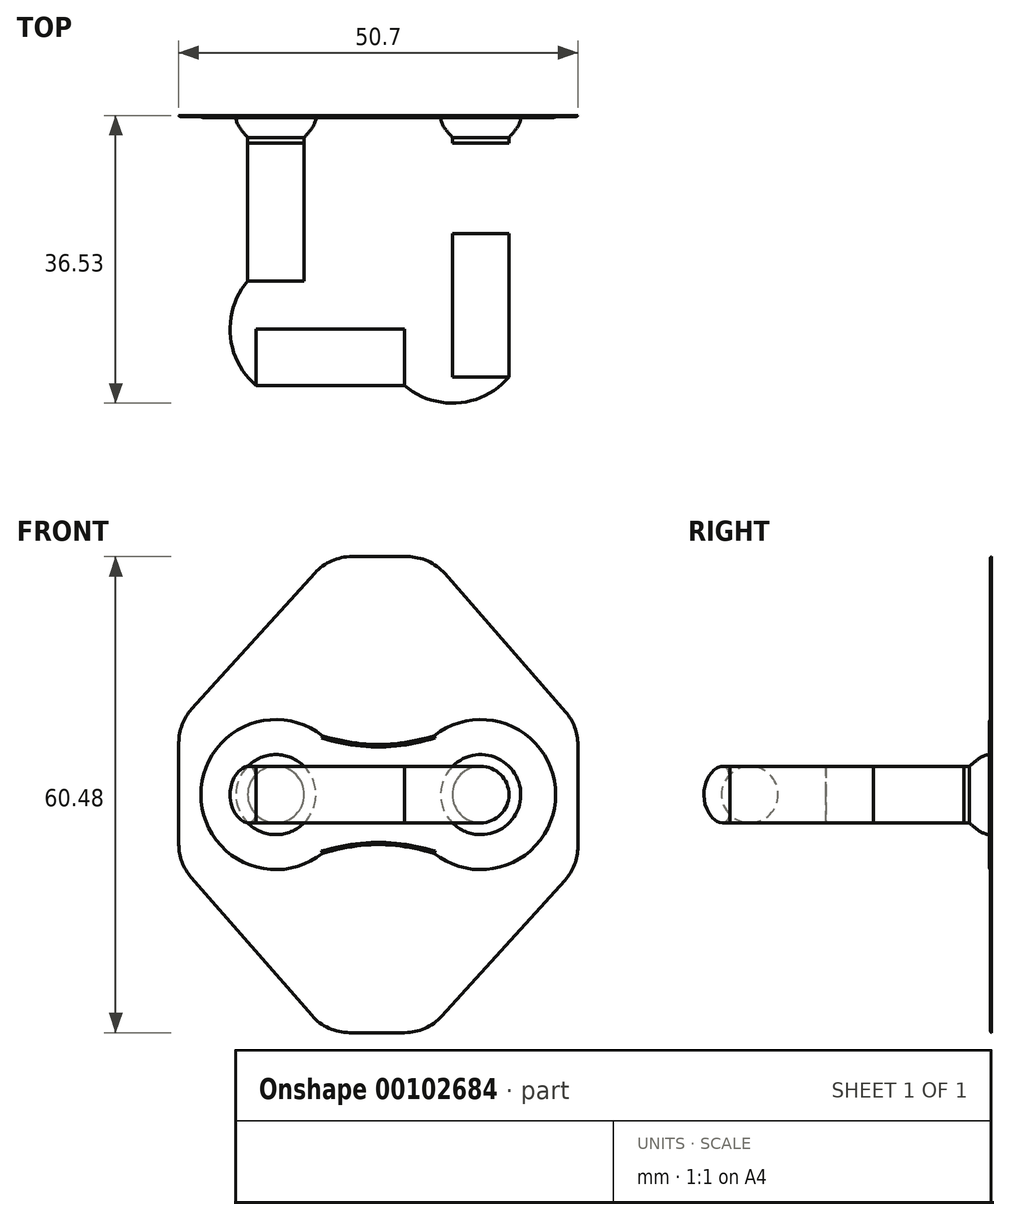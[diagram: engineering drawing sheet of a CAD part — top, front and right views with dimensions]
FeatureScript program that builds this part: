
annotation { "Feature Type Name" : "Feature", "Feature Type Description" : "" }
export const myFeature = defineFeature(function(context is Context, id is Id, definition is map)
    precondition{}
    {
        {
            var Q0;
            Q0=qCreatedBy(makeId("Front.planeOp"),FACE);
            var sketch = newSketch(context, id + "F0", { "sketchPlane" : qUnion([Q0])});
            skLineSegment(sketch, "E0.bottom", {"start": v(-25.35, 30.24) * mm, "end": v(-6.16, 30.24) * mm, "construction": true});
            skLineSegment(sketch, "E0.top", {"start": v(-25.35, -30.24) * mm, "end": v(-6.54, -30.24) * mm, "construction": true});
            skLineSegment(sketch, "E0.left", {"start": v(-25.35, 30.24) * mm, "end": v(-25.35, 9.06) * mm, "construction": true});
            skLineSegment(sketch, "E0.right", {"start": v(25.35, 30.24) * mm, "end": v(25.35, 8.72) * mm, "construction": true});
            skLineSegment(sketch, "E1", {"start": v(-25.35, 30.24) * mm, "end": v(-16.12, 19.24) * mm, "construction": true});
            skLineSegment(sketch, "E2", {"start": v(25.35, 30.24) * mm, "end": v(16.14, 19.25) * mm, "construction": true});
            skLineSegment(sketch, "E3", {"start": v(0, 0) * mm, "end": v(16.12, -19.24) * mm});
            skLineSegment(sketch, "E4", {"start": v(6.54, 30.24) * mm, "end": v(25.35, 30.24) * mm, "construction": true});
            skLineSegment(sketch, "E5", {"start": v(25.35, 6.34) * mm, "end": v(25.35, -6.61) * mm});
            skLineSegment(sketch, "E6", {"start": v(8.44, 28.06) * mm, "end": v(16.14, 19.25) * mm});
            skLineSegment(sketch, "E7", {"start": v(-3.34, 30.24) * mm, "end": v(3.66, 30.24) * mm});
            skLineSegment(sketch, "E8", {"start": v(-25.35, 6.61) * mm, "end": v(-25.35, -6.34) * mm});
            skLineSegment(sketch, "E9", {"start": v(-25.35, -8.72) * mm, "end": v(-25.35, -30.24) * mm, "construction": true});
            skLineSegment(sketch, "E10", {"start": v(-3.66, -30.24) * mm, "end": v(3.34, -30.24) * mm});
            skLineSegment(sketch, "E11", {"start": v(6.16, -30.24) * mm, "end": v(25.35, -30.24) * mm, "construction": true});
            skLineSegment(sketch, "E12", {"start": v(25.35, -9.06) * mm, "end": v(25.35, -30.24) * mm, "construction": true});
            skLineSegment(sketch, "E13", {"start": v(-8.05, 28.15) * mm, "end": v(-16.12, 19.24) * mm});
            skLineSegment(sketch, "E14", {"start": v(-23.78, -10.51) * mm, "end": v(-8.44, -28.06) * mm});
            skLineSegment(sketch, "E15", {"start": v(8.05, -28.15) * mm, "end": v(23.7, -10.88) * mm});
            skLineSegment(sketch, "E16", {"start": v(16.12, -19.24) * mm, "end": v(25.35, -30.24) * mm, "construction": true});
            skLineSegment(sketch, "E17", {"start": v(16.14, 19.25) * mm, "end": v(23.78, 10.51) * mm});
            skLineSegment(sketch, "E18", {"start": v(-16.12, 19.24) * mm, "end": v(-23.7, 10.88) * mm});
            skLineSegment(sketch, "E19", {"start": v(-16.14, -19.25) * mm, "end": v(-25.35, -30.24) * mm, "construction": true});
            skLineSegment(sketch, "E20", {"start": v(-16.12, 19.24) * mm, "end": v(0, 0) * mm});
            skLineSegment(sketch, "E21", {"start": v(16.14, 19.25) * mm, "end": v(-16.14, -19.25) * mm});
            skPoint(sketch, "E22.visualSharp", {"position": v(-6.16, 30.24) * mm});
            skArc(sketch, "E22.filletArc", {"start": v(-3.34, 30.24) * mm, "mid": v(-5.92, 29.7) * mm, "end": v(-8.05, 28.15) * mm});
            skPoint(sketch, "E23.visualSharp", {"position": v(6.54, 30.24) * mm});
            skArc(sketch, "E23.filletArc", {"start": v(8.44, 28.06) * mm, "mid": v(6.28, 29.67) * mm, "end": v(3.66, 30.24) * mm});
            skPoint(sketch, "E24.visualSharp", {"position": v(25.35, 8.72) * mm});
            skArc(sketch, "E24.filletArc", {"start": v(25.35, 6.34) * mm, "mid": v(24.94, 8.57) * mm, "end": v(23.78, 10.51) * mm});
            skPoint(sketch, "E25.visualSharp", {"position": v(25.35, -9.06) * mm});
            skArc(sketch, "E25.filletArc", {"start": v(23.7, -10.88) * mm, "mid": v(24.92, -8.9) * mm, "end": v(25.35, -6.61) * mm});
            skPoint(sketch, "E26.visualSharp", {"position": v(6.16, -30.24) * mm});
            skArc(sketch, "E26.filletArc", {"start": v(3.34, -30.24) * mm, "mid": v(5.92, -29.7) * mm, "end": v(8.05, -28.15) * mm});
            skPoint(sketch, "E27.visualSharp", {"position": v(-6.54, -30.24) * mm});
            skArc(sketch, "E27.filletArc", {"start": v(-8.44, -28.06) * mm, "mid": v(-6.28, -29.67) * mm, "end": v(-3.66, -30.24) * mm});
            skPoint(sketch, "E28.visualSharp", {"position": v(-25.35, -8.72) * mm});
            skArc(sketch, "E28.filletArc", {"start": v(-25.35, -6.34) * mm, "mid": v(-24.94, -8.57) * mm, "end": v(-23.78, -10.51) * mm});
            skPoint(sketch, "E29.visualSharp", {"position": v(-25.35, 9.06) * mm});
            skArc(sketch, "E29.filletArc", {"start": v(-23.7, 10.88) * mm, "mid": v(-24.92, 8.9) * mm, "end": v(-25.35, 6.61) * mm});
            skSolve(sketch);
        }
        {
            assignVariable(context, id + "F1", {"name" : "RealDistance", "anyValue" : .15});
        }
        {
            var Q0;
            Q0 = qSketchRegion(id + "F0", true);
            extrude(context, id + "F2", {"entities" : qUnion([Q0]), "depth" : (getVariable(context, 'RealDistance')) * mm});
        }
        {
            assignVariable(context, id + "F3", {"name" : "FilletBase", "anyValue" : .5});
        }
        {
            var Q0;
            Q0=makeQuery(id+"F2.opExtrude","CAP_EDGE",EDGE,{"disambiguationData":[OSD([sQuery(id+"F0.wireOp",EDGE,"E5")])],"isStart":false});
            fillet(context, id + "F4", {"entities" : qUnion([Q0]), "radius" : (getVariable(context, 'FilletBase')) * mm, "tangentPropagation" : true, "allowEdgeOverflow" : false});
        }
        {
            var Q0;
            Q0=makeQuery(id+"F2.opExtrude","CAP_FACE",FACE,{"disambiguationData":[OSD([sQuery(id+"F0.wireOp",EDGE,"E5"),sQuery(id+"F0.wireOp",EDGE,"E6"),sQuery(id+"F0.wireOp",EDGE,"E7"),sQuery(id+"F0.wireOp",EDGE,"E8"),sQuery(id+"F0.wireOp",EDGE,"E10"),sQuery(id+"F0.wireOp",EDGE,"E13"),sQuery(id+"F0.wireOp",EDGE,"E14"),sQuery(id+"F0.wireOp",EDGE,"E15"),sQuery(id+"F0.wireOp",EDGE,"E17"),sQuery(id+"F0.wireOp",EDGE,"E18"),sQuery(id+"F0.wireOp",EDGE,"E22.filletArc"),sQuery(id+"F0.wireOp",EDGE,"E23.filletArc"),sQuery(id+"F0.wireOp",EDGE,"E24.filletArc"),sQuery(id+"F0.wireOp",EDGE,"E25.filletArc"),sQuery(id+"F0.wireOp",EDGE,"E26.filletArc"),sQuery(id+"F0.wireOp",EDGE,"E27.filletArc"),sQuery(id+"F0.wireOp",EDGE,"E28.filletArc"),sQuery(id+"F0.wireOp",EDGE,"E29.filletArc")])],"isStart":false});
            var sketch = newSketch(context, id + "F5", { "sketchPlane" : qUnion([Q0])});
            skCircle(sketch, "E30", {"center": v(-13, 0) * mm, "radius": 9.53 * mm});
            skCircle(sketch, "E31", {"center": v(13, 0) * mm, "radius": 9.53 * mm});
            skLineSegment(sketch, "E32", {"start": v(0, 6.35) * mm, "end": v(0, -6.35) * mm, "construction": true});
            skLineSegment(sketch, "E33", {"start": v(-13, 9.52) * mm, "end": v(0, 9.52) * mm, "construction": true});
            skLineSegment(sketch, "E34", {"start": v(-13, -9.53) * mm, "end": v(0, -9.53) * mm, "construction": true});
            skLineSegment(sketch, "E35", {"start": v(-13, 9.53) * mm, "end": v(-13, 0) * mm, "construction": true});
            skLineSegment(sketch, "E36", {"start": v(-13, 0) * mm, "end": v(-13, -9.53) * mm, "construction": true});
            skLineSegment(sketch, "E37", {"start": v(13, -9.53) * mm, "end": v(13, 0) * mm, "construction": true});
            skLineSegment(sketch, "E38", {"start": v(13, 9.53) * mm, "end": v(13, 0) * mm, "construction": true});
            skLineSegment(sketch, "E39", {"start": v(0, 9.52) * mm, "end": v(13, 9.52) * mm, "construction": true});
            skLineSegment(sketch, "E40", {"start": v(0, -9.53) * mm, "end": v(13, -9.53) * mm, "construction": true});
            skFitSpline(sketch, "E41", {"points": [v(-13, 9.53) * mm, v(0, 6.35) * mm, v(13, 9.52) * mm], "startDerivative": vector(24.13, -9.53) * mm, "endDerivative": vector(24.13, 9.52) * mm});
            skFitSpline(sketch, "E42", {"points": [v(-13, -9.53) * mm, v(0, -6.35) * mm, v(13, -9.53) * mm], "startDerivative": vector(24.13, 9.53) * mm, "endDerivative": vector(24.13, -9.53) * mm});
            skSolve(sketch);
        }
        {
            assignVariable(context, id + "F6", {"name" : "RealDistancePlatform", "anyValue" : .1});
        }
        {
            var Q0;
            Q0 = qSketchRegion(id + "F5", true);
            extrude(context, id + "F7", {"entities" : qUnion([Q0]), "operationType" : NewBodyOperationType.ADD, "depth" : (getVariable(context, 'RealDistancePlatform')) * mm});
        }
        {
            var Q0;
            Q0=makeQuery(id+"F7.opExtrude","CAP_EDGE",EDGE,{"disambiguationData":[OSD([sQuery(id+"F5.wireOp",EDGE,"E31")])],"isStart":false});
            var Q1;
            Q1=makeQuery(id+"F7.opExtrude","CAP_EDGE",EDGE,{"disambiguationData":[OSD([sQuery(id+"F5.wireOp",EDGE,"E42")])],"isStart":false});
            var Q2;
            Q2=makeQuery(id+"F7.opExtrude","CAP_EDGE",EDGE,{"disambiguationData":[OSD([sQuery(id+"F5.wireOp",EDGE,"E30")])],"isStart":false});
            var Q3;
            Q3=makeQuery(id+"F7.opExtrude","CAP_EDGE",EDGE,{"disambiguationData":[OSD([sQuery(id+"F5.wireOp",EDGE,"E41")])],"isStart":false});
            fillet(context, id + "F8", {"entities" : qUnion([Q0, Q1, Q2, Q3]), "radius" : (getVariable(context, 'FilletBase')) * mm, "tangentPropagation" : true, "allowEdgeOverflow" : false});
        }
        {
            var Q0;
            Q0=makeQuery(id+"F7.opExtrude","CAP_FACE",FACE,{"disambiguationData":[OSD([sQuery(id+"F5.wireOp",EDGE,"E30"),sQuery(id+"F5.wireOp",EDGE,"E31"),sQuery(id+"F5.wireOp",EDGE,"E41"),sQuery(id+"F5.wireOp",EDGE,"E42")])],"isStart":false});
            var sketch = newSketch(context, id + "F9", { "sketchPlane" : qUnion([Q0])});
            skCircle(sketch, "E43", {"center": v(-13, 0) * mm, "radius": 5.08 * mm});
            skCircle(sketch, "E44", {"center": v(13, 0) * mm, "radius": 5.08 * mm});
            skSolve(sketch);
        }
        {
            var Q0;
            Q0=makeQuery(id+"F9.imprint","IMPRINT",FACE,{"disambiguationData":[TD([[makeQuery(id+"F9.imprint","IMPRINT",EDGE,{"derivedFrom":sQuery(id+"F9.wireOp",EDGE,"E43")}),-1.0]])]});
            cPlane(context, id + "F10", {"entities" : qUnion([Q0]), "cplaneType" : CPlaneType.OFFSET, "offset" : 2.54 * mm, "width" : 152.4 * mm, "height" : 152.4 * mm});
        }
        {
            var Q0;
            Q0=qCreatedBy(id+"F10.planeOp",FACE);
            var sketch = newSketch(context, id + "F11", { "sketchPlane" : qUnion([Q0])});
            skCircle(sketch, "E45", {"center": v(-13, 0) * mm, "radius": 3.6 * mm});
            skCircle(sketch, "E46", {"center": v(13, 0) * mm, "radius": 3.6 * mm});
            skSolve(sketch);
        }
        {
            var Q0;
            Q0=makeQuery(id+"F9.imprint","IMPRINT",FACE,{"disambiguationData":[TD([[makeQuery(id+"F9.imprint","IMPRINT",EDGE,{"derivedFrom":sQuery(id+"F9.wireOp",EDGE,"E43")}),1.0]])]});
            var Q1;
            Q1=makeQuery(id+"F11.imprint","IMPRINT",FACE,{"disambiguationData":[TD([[makeQuery(id+"F11.imprint","IMPRINT",EDGE,{"derivedFrom":sQuery(id+"F11.wireOp",EDGE,"E45")}),1.0]])]});
            loft(context, id + "F12", {"startCondition" : LoftEndDerivativeType.NORMAL_TO_PROFILE, "startMagnitude" : 1, "sheetProfilesArray" : [{ "sheetProfileEntities" : qUnion([Q0]) }, { "sheetProfileEntities" : qUnion([Q1]) }]});
        }
        {
            var Q1;
            Q1=makeQuery(id+"F9.imprint","IMPRINT",FACE,{"disambiguationData":[TD([[makeQuery(id+"F9.imprint","IMPRINT",EDGE,{"derivedFrom":sQuery(id+"F9.wireOp",EDGE,"E44")}),1.0]])]});
            var Q2;
            Q2=makeQuery(id+"F11.imprint","IMPRINT",FACE,{"disambiguationData":[TD([[makeQuery(id+"F11.imprint","IMPRINT",EDGE,{"derivedFrom":sQuery(id+"F11.wireOp",EDGE,"E46")}),1.0]])]});
            loft(context, id + "F13", {"operationType" : NewBodyOperationType.ADD, "startCondition" : LoftEndDerivativeType.NORMAL_TO_PROFILE, "startMagnitude" : 1, "sheetProfilesArray" : [{ "sheetProfileEntities" : qUnion([Q1]) }, { "sheetProfileEntities" : qUnion([Q2]) }]});
        }
        {
            assignVariable(context, id + "F14", {"name" : "ExLockBar", "anyValue" : .7172});
        }
        {
            var Q0;
            Q0=makeQuery(id+"F13.opLoft","CAP_FACE",FACE,{"disambiguationData":[OSD([makeQuery(id+"F11.imprint","IMPRINT",FACE,{"disambiguationData":[TD([[makeQuery(id+"F11.imprint","IMPRINT",EDGE,{"derivedFrom":sQuery(id+"F11.wireOp",EDGE,"E46")}),1.0]])]})])],"isStart":true});
            var Q1;
            Q1=makeQuery(id+"F12.opLoft","CAP_FACE",FACE,{"disambiguationData":[OSD([makeQuery(id+"F11.imprint","IMPRINT",FACE,{"disambiguationData":[TD([[makeQuery(id+"F11.imprint","IMPRINT",EDGE,{"derivedFrom":sQuery(id+"F11.wireOp",EDGE,"E45")}),1.0]])]})])],"isStart":true});
            extrude(context, id + "F15", {"entities" : qUnion([Q0, Q1]), "depth" : (getVariable(context, 'ExLockBar')) * mm});
        }
        {
            var Q0;
            Q0=qCreatedBy(makeId("Top.planeOp"),FACE);
            var sketch = newSketch(context, id + "F16", { "sketchPlane" : qUnion([Q0])});
            skLineSegment(sketch, "E47", {"start": v(-9.41, -8.9) * mm, "end": v(-9.41, -27.1) * mm, "construction": true});
            skLineSegment(sketch, "E48", {"start": v(-16.6, -27.1) * mm, "end": v(-16.6, -8.9) * mm, "construction": true});
            skLineSegment(sketch, "E49", {"start": v(16.6, -8.9) * mm, "end": v(16.6, -27.1) * mm, "construction": true});
            skLineSegment(sketch, "E50", {"start": v(9.41, -27.1) * mm, "end": v(9.41, -8.9) * mm, "construction": true});
            skLineSegment(sketch, "E51", {"start": v(-16.6, -27.1) * mm, "end": v(-13, -27.1) * mm});
            skLineSegment(sketch, "E52", {"start": v(9.41, -27.1) * mm, "end": v(13, -27.1) * mm});
            skLineSegment(sketch, "E53", {"start": v(9.41, -27.1) * mm, "end": v(4.7, -27.1) * mm});
            skLineSegment(sketch, "E54", {"start": v(-13, -27.1) * mm, "end": v(-9.41, -27.1) * mm});
            skLineSegment(sketch, "E55", {"start": v(13, -27.1) * mm, "end": v(16.6, -27.1) * mm});
            skLineSegment(sketch, "E56", {"start": v(0, -27.1) * mm, "end": v(-4.7, -27.1) * mm});
            skLineSegment(sketch, "E57", {"start": v(-9.41, -8.9) * mm, "end": v(9.41, -8.9) * mm});
            skLineSegment(sketch, "E58", {"start": v(0, -27.1) * mm, "end": v(0, -31.05) * mm});
            skLineSegment(sketch, "E59", {"start": v(-16.6, -8.9) * mm, "end": v(-13, -8.9) * mm, "construction": true});
            skLineSegment(sketch, "E60", {"start": v(16.6, -8.9) * mm, "end": v(13, -8.9) * mm, "construction": true});
            skLineSegment(sketch, "E61", {"start": v(-13, -8.9) * mm, "end": v(-9.41, -8.9) * mm, "construction": true});
            skLineSegment(sketch, "E62", {"start": v(13, -8.9) * mm, "end": v(9.41, -8.9) * mm, "construction": true});
            skLineSegment(sketch, "E63", {"start": v(-13, -27.1) * mm, "end": v(-13, -8.9) * mm});
            skLineSegment(sketch, "E64", {"start": v(13, -27.1) * mm, "end": v(13, -18) * mm});
            skLineSegment(sketch, "E65", {"start": v(13, -18) * mm, "end": v(13, -8.9) * mm});
            skLineSegment(sketch, "E66", {"start": v(-4.7, -27.1) * mm, "end": v(-9.41, -27.1) * mm});
            skLineSegment(sketch, "E67", {"start": v(4.7, -27.1) * mm, "end": v(0, -27.1) * mm});
            skLineSegment(sketch, "E68", {"start": v(-9.41, -27.1) * mm, "end": v(-9.41, -31.05) * mm});
            skLineSegment(sketch, "E69", {"start": v(9.41, -27.1) * mm, "end": v(9.41, -31.05) * mm});
            skArc(sketch, "E70", {"start": v(13, -27.1) * mm, "mid": v(11.95, -29.65) * mm, "end": v(9.41, -30.7) * mm});
            skArc(sketch, "E71", {"start": v(-13, -27.1) * mm, "mid": v(-11.95, -29.65) * mm, "end": v(-9.41, -30.7) * mm});
            skLineSegment(sketch, "E72", {"start": v(9.41, -30.7) * mm, "end": v(-9.41, -30.7) * mm});
            skSolve(sketch);
        }
        {
            var Q0;
            Q0=makeQuery(id+"F11.imprint","IMPRINT",FACE,{"disambiguationData":[TD([[makeQuery(id+"F11.imprint","IMPRINT",EDGE,{"derivedFrom":sQuery(id+"F11.wireOp",EDGE,"E45")}),1.0]])]});
            var Q1;
            Q1=sQuery(id+"F16.wireOp",EDGE,"E63");
            var Q2;
            Q2=sQuery(id+"F16.wireOp",EDGE,"E71");
            var Q3;
            Q3=sQuery(id+"F16.wireOp",EDGE,"E72");
            var Q4;
            Q4=sQuery(id+"F16.wireOp",EDGE,"E70");
            var Q5;
            Q5=sQuery(id+"F16.wireOp",EDGE,"E64");
            var Q6;
            Q6=sQuery(id+"F16.wireOp",EDGE,"E65");
            sweep(context, id + "F17", {"profiles" : qUnion([Q0]), "path" : qUnion([Q1, Q2, Q3, Q4, Q5, Q6])});
        }
    });
